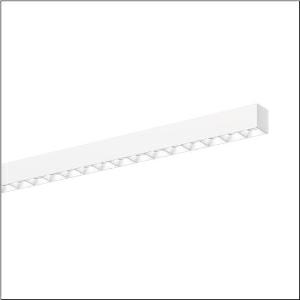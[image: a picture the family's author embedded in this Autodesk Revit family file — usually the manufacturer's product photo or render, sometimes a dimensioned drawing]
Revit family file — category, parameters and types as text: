
# Revit family: silica_r__21_51mx26dc3awb_8cf9
name_source: partatom
category: Lighting Fixtures
units: mm (PartAtom-declared; Revit-internal decimal feet)

## family parameters
Cut with Voids When Loaded = No
Host = Face
Light Source = No
Part Type = Normal
Room Calculation Point = No
Round Connector Dimension = Use Diameter
Shared = No

## types (1)
- --- (1 x LED, 10800 lm, 63.6 W, 3000K)
    Apparent Load = 64 VA
    CIE Flux Codes = 83 98 100 100 100
    Color Rendering = 80
    Color Temperature = 3000K
    Default Elevation = 1800 mm
    Description = Silica® 21, office luminaire, primary light control with darklight reflector, of PMMA, white, CAT 2 (L<= 3000cd/m²), light emission: direct distribution, primary light characteristic: symmetric, installation type: surface-mounted, LED, rated luminous flux: 10.800lm, luminous efficacy: 170lm/W, light colour: 830, colour temperature: 3000K, with terminal, 3+2-pole, max. 2.5mm², mains connection: 220..240V, AC, 50/60Hz, rated input power: 63.6W, luminaire housing, of aluminium, traffic white (RAL 9016), length: 3.004mm, width: 53mm, height: 53mm, protection rating (complete): IP20, insulation class (complete): insulation class I (protective earthing), certification: CE, permissible operating ambient temperature: 0..+35°C, standard: EN 50419, packaging unit: 1 piece
    Height = 0 mm  [stored 0 ft]
    Lamp = 1 x LED
    Lamp Light Flux = 10800 lm
    Lamp Power = 63.6 W
    Lamp count = 1
    Length = 3004 mm
    Luminous efficacy = 170 lm/W
    Manufacturer = Siteco
    ModVariant = No
    Model = 51MX26DC3AWB
    Mounting Place = Ceiling
    Mounting Type = Recessed
    Number of Poles = 1
    OnlyDefault = Yes
    Power Factor = 1
    Product Name = Silica® 21
    Product group = office luminaire | ceiling recessed
    ProductGroupID = 400
    Protection Class = Protection class I
    Protection Degree = IP 20
    RLX_Detail_Level = 1
    RLX_Emergency_Light_Flux = 0 lm
    RLX_Emergency_Type = 0
    RLX_Emergency_Type_DB = No
    RlxData = <blob elided: 58989 chars, md5=99a7133c>
    Socket = socket
    Standby Power = 0 W
    System Light Flux = 10800 lm
    System Power = 64 W
    Type Comments = factory setting: luminous flux: 100 % | dim-lin: 254 | 360 mA
    Type Image = l_1335934.jpg
    URL = http://relux.com
    VarID = @adj_094091
    Voltage = 0 V
    Weight = 0.00 kg
    Width = 53 mm

note: [stored X ft] marks values corroborated as IEEE doubles in the binary element streams (Revit-internal decimal feet)

## geometry (parser evidence)
native form markers: Blend x4, Sweep x12
no freeform markers — native parametric forms only
